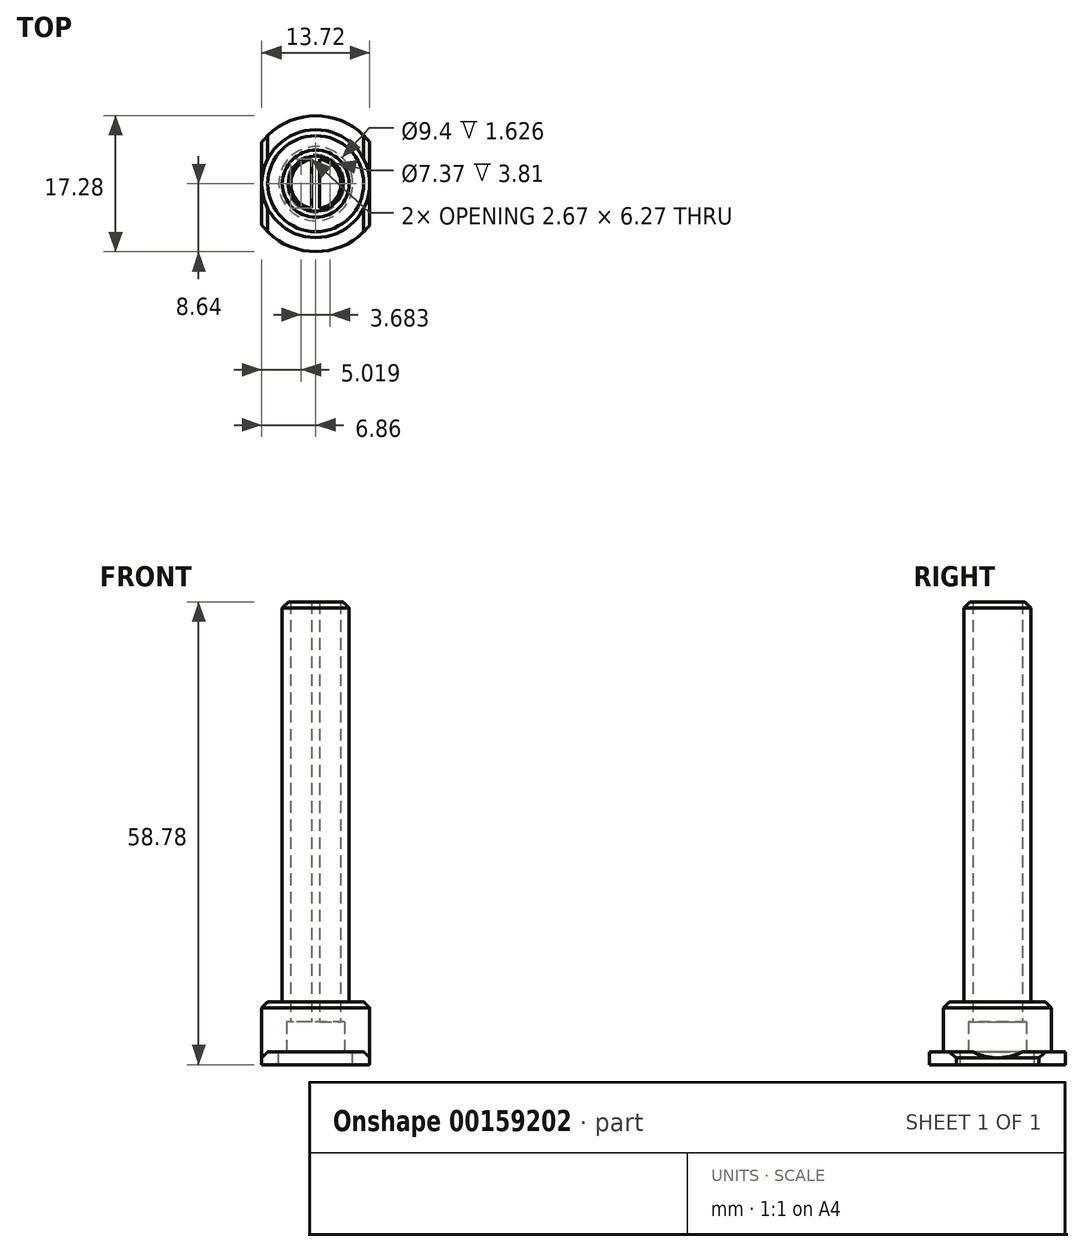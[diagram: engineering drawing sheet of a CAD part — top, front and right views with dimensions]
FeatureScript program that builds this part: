
annotation { "Feature Type Name" : "Feature", "Feature Type Description" : "" }
export const myFeature = defineFeature(function(context is Context, id is Id, definition is map)
    precondition{}
    {
        {
            var Q0;
            Q0=qCreatedBy(makeId("Top.planeOp"),FACE);
            var sketch = newSketch(context, id + "F0", { "sketchPlane" : qUnion([Q0])});
            skCircle(sketch, "E0", {"center": v(0, 0) * mm, "radius": 8.64 * mm});
            skCircle(sketch, "E1", {"center": v(0, 0) * mm, "radius": 4.7 * mm});
            skLineSegment(sketch, "E2", {"start": v(0, -3.68) * mm, "end": v(0, -3.68) * mm});
            skLineSegment(sketch, "E3", {"start": v(0, 3.68) * mm, "end": v(0, 3.68) * mm});
            skLineSegment(sketch, "E4", {"start": v(0, -3.68) * mm, "end": v(0, 3.68) * mm});
            skArc(sketch, "E5", {"start": v(0, -3.68) * mm, "mid": v(3.68, 0) * mm, "end": v(0, 3.68) * mm});
            skArc(sketch, "E6", {"start": v(0, 3.68) * mm, "mid": v(-3.68, 0) * mm, "end": v(0, -3.68) * mm});
            skLineSegment(sketch, "E7.0", {"start": v(-0.5, -3.13) * mm, "end": v(-0.5, 3.13) * mm});
            skArc(sketch, "E7.1", {"start": v(-0.5, 3.13) * mm, "mid": v(-3.17, 0) * mm, "end": v(-0.5, -3.13) * mm});
            skLineSegment(sketch, "E8.MirrorCS", {"start": v(0.5, -3.13) * mm, "end": v(0.5, 3.13) * mm});
            skArc(sketch, "E9.MirrorCS", {"start": v(0.5, 3.13) * mm, "mid": v(3.17, 0) * mm, "end": v(0.5, -3.13) * mm});
            skLineSegment(sketch, "E10", {"start": v(6.86, -5.25) * mm, "end": v(6.86, 5.25) * mm});
            skLineSegment(sketch, "E11.MirrorCS", {"start": v(-6.86, -5.25) * mm, "end": v(-6.86, 5.25) * mm});
            skSolve(sketch);
        }
        {
            var Q0;
            Q0=makeQuery(id+"F0.imprint","IMPRINT",FACE,{"disambiguationData":[TD([[makeQuery(id+"F0.imprint","IMPRINT",EDGE,{"derivedFrom":sQuery(id+"F0.wireOp",EDGE,"E1")}),-1.0]])]});
            extrude(context, id + "F1", {"entities" : qUnion([Q0]), "oppositeDirection" : true, "depth" : 1.63 * mm});
        }
        {
            var Q0;
            Q0=makeQuery(id+"F0.imprint","IMPRINT",FACE,{"disambiguationData":[TD([[makeQuery(id+"F0.imprint","IMPRINT",EDGE,{"derivedFrom":sQuery(id+"F0.wireOp",EDGE,"E1")}),-1.0]])]});
            var sketch = newSketch(context, id + "F2", { "sketchPlane" : qUnion([Q0])});
            skLineSegment(sketch, "E12.0", {"start": v(-6.86, -5.25) * mm, "end": v(-6.86, 5.25) * mm});
            skLineSegment(sketch, "E13.0", {"start": v(6.86, -5.25) * mm, "end": v(6.86, 5.25) * mm});
            skCircle(sketch, "E14", {"center": v(0, 0) * mm, "radius": 6.86 * mm});
            skArc(sketch, "E15.0", {"start": v(0, -3.68) * mm, "mid": v(3.68, 0) * mm, "end": v(0, 3.68) * mm});
            skArc(sketch, "E16.0", {"start": v(0, 3.68) * mm, "mid": v(-3.68, 0) * mm, "end": v(0, -3.68) * mm});
            skSolve(sketch);
        }
        {
            var Q0;
            Q0 = qSketchRegion(id + "F2", true);
            extrude(context, id + "F3", {"entities" : qUnion([Q0]), "operationType" : NewBodyOperationType.ADD, "depth" : 3.8 * mm});
        }
        {
            var Q0;
            Q0=makeQuery(id+"F3.opExtrude","CAP_FACE",FACE,{"disambiguationData":[OSD([sQuery(id+"F2.wireOp",EDGE,"E14"),sQuery(id+"F2.wireOp",EDGE,"E15.0"),sQuery(id+"F2.wireOp",EDGE,"E16.0")])],"isStart":false});
            var sketch = newSketch(context, id + "F4", { "sketchPlane" : qUnion([Q0])});
            skLineSegment(sketch, "E17.0", {"start": v(-0.5, -3.13) * mm, "end": v(-0.5, 3.13) * mm});
            skLineSegment(sketch, "E18.0", {"start": v(0.5, -3.13) * mm, "end": v(0.5, 3.13) * mm});
            skArc(sketch, "E19.0", {"start": v(0.5, 3.13) * mm, "mid": v(3.17, 0) * mm, "end": v(0.5, -3.13) * mm});
            skArc(sketch, "E20.0", {"start": v(-0.5, 3.13) * mm, "mid": v(-3.17, 0) * mm, "end": v(-0.5, -3.13) * mm});
            skCircle(sketch, "E21.0", {"center": v(0, 0) * mm, "radius": 6.86 * mm});
            skSolve(sketch);
        }
        {
            var Q0;
            Q0 = qSketchRegion(id + "F4", true);
            extrude(context, id + "F5", {"entities" : qUnion([Q0]), "operationType" : NewBodyOperationType.ADD, "depth" : 2.54 * mm});
        }
        {
            var Q0;
            Q0=makeQuery(id+"F5.opExtrude","CAP_FACE",FACE,{"disambiguationData":[OSD([sQuery(id+"F4.wireOp",EDGE,"E17.0"),sQuery(id+"F4.wireOp",EDGE,"E18.0"),sQuery(id+"F4.wireOp",EDGE,"E19.0"),sQuery(id+"F4.wireOp",EDGE,"E20.0"),sQuery(id+"F4.wireOp",EDGE,"E21.0")])],"isStart":false});
            var sketch = newSketch(context, id + "F6", { "sketchPlane" : qUnion([Q0])});
            skLineSegment(sketch, "E22.0", {"start": v(-0.5, -3.13) * mm, "end": v(-0.5, 3.13) * mm});
            skLineSegment(sketch, "E23.0", {"start": v(0.5, -3.13) * mm, "end": v(0.5, 3.13) * mm});
            skArc(sketch, "E24.0", {"start": v(0.5, 3.13) * mm, "mid": v(3.17, 0) * mm, "end": v(0.5, -3.13) * mm});
            skArc(sketch, "E25.0", {"start": v(-0.5, 3.13) * mm, "mid": v(-3.17, 0) * mm, "end": v(-0.5, -3.13) * mm});
            skCircle(sketch, "E26", {"center": v(0, 0) * mm, "radius": 4.25 * mm});
            skSolve(sketch);
        }
        {
            var Q0;
            Q0 = qSketchRegion(id + "F6", true);
            extrude(context, id + "F7", {"entities" : qUnion([Q0]), "operationType" : NewBodyOperationType.ADD, "depth" : 50.8 * mm});
        }
        {
            var Q0;
            Q0=makeQuery(id+"F7.opExtrude","CAP_EDGE",EDGE,{"disambiguationData":[OSD([sQuery(id+"F6.wireOp",EDGE,"E26")])],"isStart":true});
            var Q1;
            Q1=makeQuery(id+"F5.opExtrude","CAP_EDGE",EDGE,{"disambiguationData":[OSD([sQuery(id+"F4.wireOp",EDGE,"E21.0")])],"isStart":false});
            var Q2;
            {var subQ0=sQuery(id+"F0.wireOp",EDGE,"E11.MirrorCS");var subQ1=sQuery(id+"F0.wireOp",EDGE,"E10");var subQ2=sQuery(id+"F0.wireOp",EDGE,"E0");Q2=makeQuery(id+"F3.boolean.opBoolean","SPLIT",EDGE,{"disambiguationData":[TD([makeQuery(id+"F1.opExtrude","SWEPT_FACE",FACE,{"disambiguationData":[OSD([subQ2]),TDD([makeQuery(id+"F0.imprint","IMPRINT",EDGE,{"disambiguationData":[TD([[makeQuery(id+"F0.imprint","INTERSECT",VERTEX,{"disambiguationData":[OD(0.0)],"derivedFrom":[subQ2,subQ1]}),1.0]])],"derivedFrom":subQ2})])]})])],"derivedFrom":makeQuery(id+"F1.opExtrude","CAP_EDGE",EDGE,{"disambiguationData":[OSD([subQ0])],"isStart":true})});}
            var Q3;
            {var subQ1=sQuery(id+"F0.wireOp",EDGE,"E10");var subQ2=sQuery(id+"F0.wireOp",EDGE,"E0");Q3=makeQuery(id+"F3.boolean.opBoolean","SPLIT",EDGE,{"disambiguationData":[TD([makeQuery(id+"F1.opExtrude","SWEPT_FACE",FACE,{"disambiguationData":[OSD([subQ2]),TDD([makeQuery(id+"F0.imprint","IMPRINT",EDGE,{"disambiguationData":[TD([[makeQuery(id+"F0.imprint","INTERSECT",VERTEX,{"disambiguationData":[OD(0.0)],"derivedFrom":[subQ2,subQ1]}),1.0]])],"derivedFrom":subQ2})])]})])],"derivedFrom":makeQuery(id+"F1.opExtrude","CAP_EDGE",EDGE,{"disambiguationData":[OSD([subQ1])],"isStart":true})});}
            var Q4;
            Q4=makeQuery(id+"F7.opExtrude","CAP_EDGE",EDGE,{"disambiguationData":[OSD([sQuery(id+"F6.wireOp",EDGE,"E26")])],"isStart":false});
            chamfer(context, id + "F8", {"entities" : qUnion([Q0, Q1, Q2, Q3, Q4]), "width" : 0.76 * mm, "tangentPropagation" : true});
        }
    });
